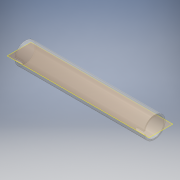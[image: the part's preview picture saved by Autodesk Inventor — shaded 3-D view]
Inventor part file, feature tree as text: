
AUTODESK INVENTOR PART (.ipt)
format: ipt  version: 2016 (Build 200138000, 138)  size: 144,384 bytes
history: native  units: mm
features: extrude x2, plane x2, sketch x2, fillet x1, mirror x1
ambient origin geometry x8: Origin, YZ Plane, XZ Plane, XY Plane, X Axis, Y Axis, Z Axis, Center Point
bodies: Solid1 (feature_tree)
feature tree (8):
  extrude  "Extrusion1"  Depth=26.0mm
  extrude  "Extrusion2"  Depth=4.0mm
  fillet  "Fillet1"  Radius=11.0mm
  plane  "Work Plane1"
  mirror  "Mirror1"
  plane  "Work Plane2"
  sketch  "Sketch1"  dims[d0=30.0mm d1=26.0mm]
  sketch  "Sketch2"  dims[d2=180.0mm d3=0.0mm d4=4.0mm d5=11.0mm d6=180.0mm d7=0.0mm d8=2.0mm]
